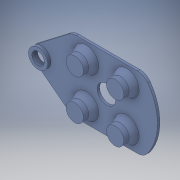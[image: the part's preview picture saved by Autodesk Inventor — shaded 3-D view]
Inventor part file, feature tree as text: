
AUTODESK INVENTOR PART (.ipt)
format: ipt  version: 2019 (Build 230136000, 136)  size: 202,752 bytes
history: native  units: mm
features: extrude x5, sketch x5, chamfer x4, fillet x2
ambient origin geometry x8: Origin, YZ Plane, XZ Plane, XY Plane, X Axis, Y Axis, Z Axis, Center Point
bodies: Solide1 (feature_tree)
feature tree (16):
  extrude  "Extrusion1"  Depth=6.2mm
  fillet  "Congé1"  Radius=23.0mm
  fillet  "Congé2"  Radius=23.0mm
  extrude  "Extrusion2"  Depth=23.0mm
  extrude  "Extrusion3"  Depth=11.5mm
  extrude  "Extrusion4"  Depth=11.5mm
  extrude  "Extrusion6"  Depth=9.9mm
  chamfer  "Chanfrein2"  Distance=9.9mm
  chamfer  "Chanfrein3"  Distance=19.0mm
  chamfer  "Chanfrein4"  Distance=40.5mm
  chamfer  "Chanfrein5"  Distance=4.0mm
  sketch  "Esquisse1"
  sketch  "Esquisse3"
  sketch  "Esquisse4"
  sketch  "Esquisse5"
  sketch  "Esquisse7"
